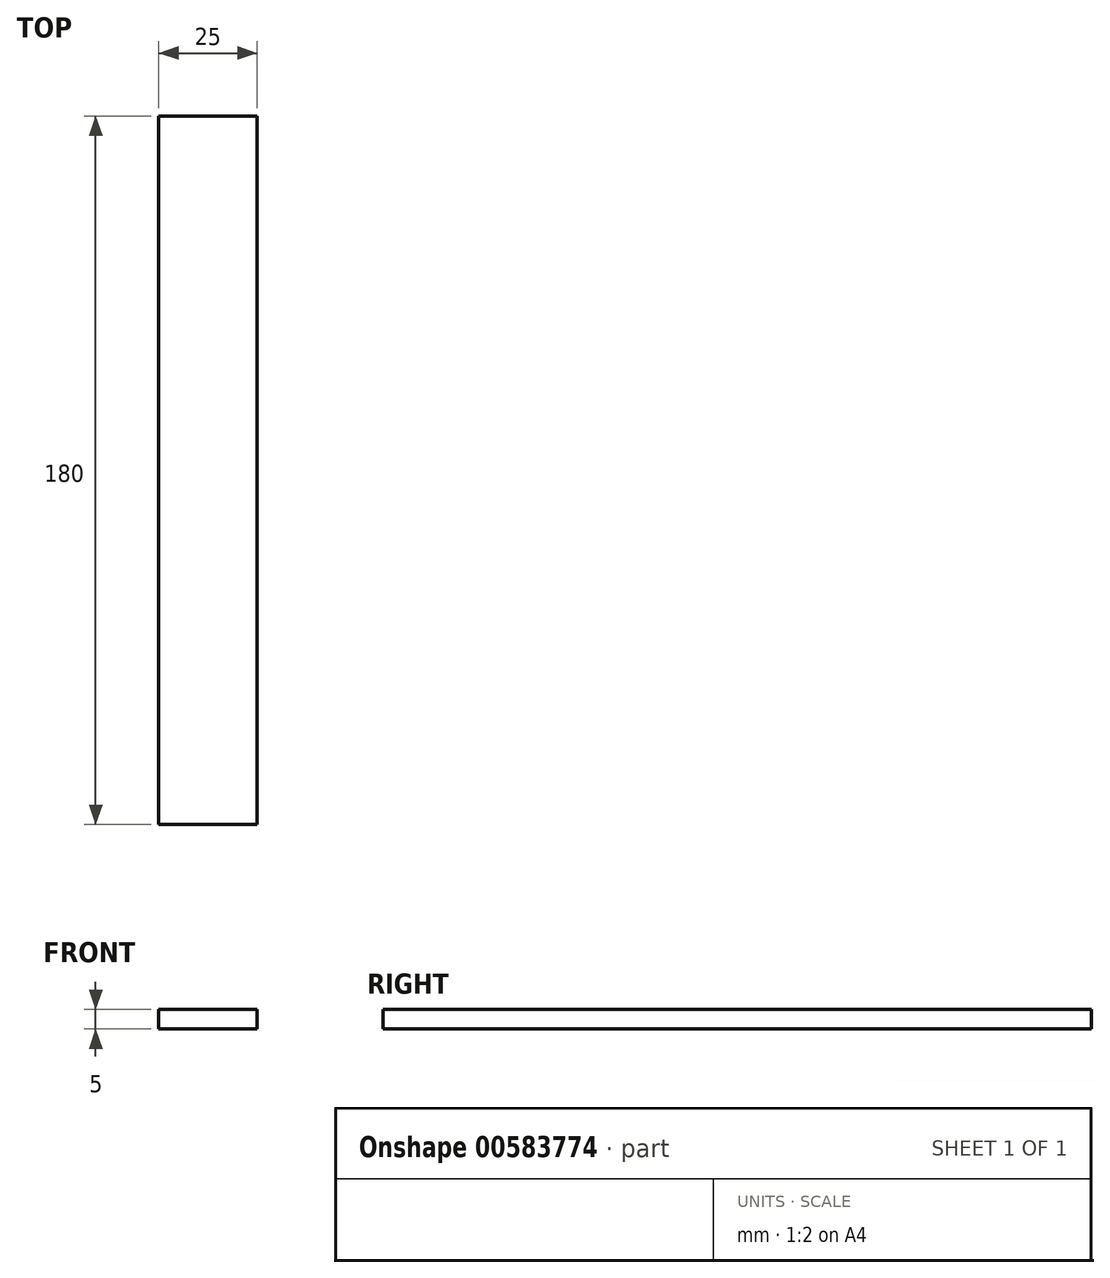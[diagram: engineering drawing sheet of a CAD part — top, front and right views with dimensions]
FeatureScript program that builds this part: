
annotation { "Feature Type Name" : "Feature", "Feature Type Description" : "" }
export const myFeature = defineFeature(function(context is Context, id is Id, definition is map)
    precondition{}
    {
        {
            var Q0;
            Q0=qCreatedBy(makeId("Front.planeOp"),FACE);
            var sketch = newSketch(context, id + "F0", { "sketchPlane" : qUnion([Q0])});
            skLineSegment(sketch, "E0.bottom", {"start": v(12.5, -2.5) * mm, "end": v(-12.5, -2.5) * mm});
            skLineSegment(sketch, "E0.top", {"start": v(12.5, 2.5) * mm, "end": v(-12.5, 2.5) * mm});
            skLineSegment(sketch, "E0.left", {"start": v(12.5, -2.5) * mm, "end": v(12.5, 2.5) * mm});
            skLineSegment(sketch, "E0.right", {"start": v(-12.5, -2.5) * mm, "end": v(-12.5, 2.5) * mm});
            skPoint(sketch, "E0.middle", {"position": v(0, 0) * mm});
            skSolve(sketch);
        }
        {
            var Q0;
            Q0=makeQuery(id+"F0.imprint","IMPRINT",FACE,{"disambiguationData":[TD([[makeQuery(id+"F0.imprint","IMPRINT",EDGE,{"derivedFrom":sQuery(id+"F0.wireOp",EDGE,"E0.bottom")}),-1.0]])]});
            extrude(context, id + "F1", {"entities" : qUnion([Q0]), "endBound" : BoundingType.SYMMETRIC, "depth" : 180 * mm, "offsetDistance" : 25 * mm});
        }
    });
